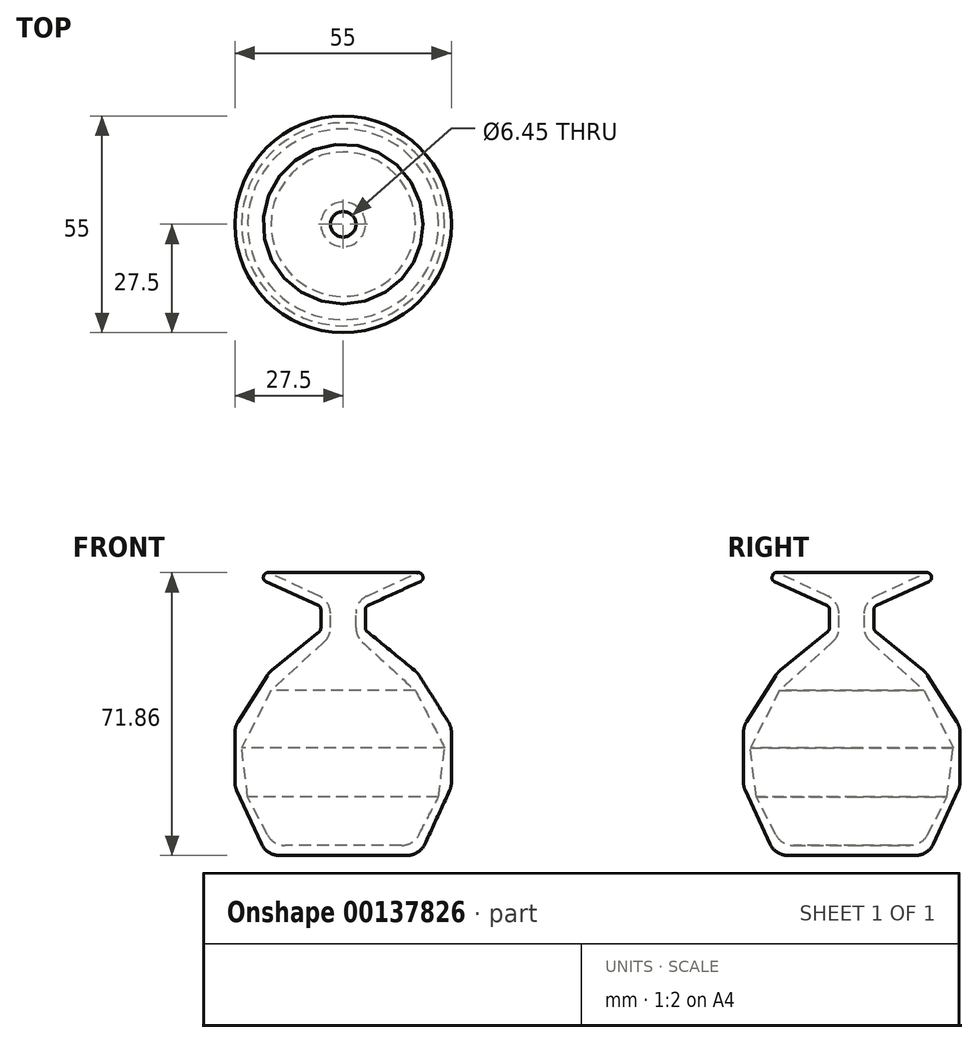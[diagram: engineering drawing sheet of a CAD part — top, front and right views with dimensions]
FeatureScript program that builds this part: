
annotation { "Feature Type Name" : "Feature", "Feature Type Description" : "" }
export const myFeature = defineFeature(function(context is Context, id is Id, definition is map)
    precondition{}
    {
        {
            var Q0;
            Q0=qCreatedBy(makeId("Front.planeOp"),FACE);
            var sketch = newSketch(context, id + "F0", { "sketchPlane" : qUnion([Q0])});
            skLineSegment(sketch, "E0", {"start": v(0, 0) * mm, "end": v(16.23, 0) * mm});
            skLineSegment(sketch, "E1", {"start": v(20.77, 2.9) * mm, "end": v(27.04, 16.49) * mm});
            skLineSegment(sketch, "E2", {"start": v(27.5, 18.58) * mm, "end": v(27.5, 31.28) * mm});
            skLineSegment(sketch, "E3", {"start": v(26.72, 33.95) * mm, "end": v(19.26, 45.78) * mm});
            skLineSegment(sketch, "E4", {"start": v(18.2, 46.99) * mm, "end": v(6.05, 56.93) * mm});
            skLineSegment(sketch, "E5", {"start": v(5.68, 57.7) * mm, "end": v(5.68, 62.57) * mm});
            skLineSegment(sketch, "E6", {"start": v(6.26, 63.48) * mm, "end": v(19.71, 69.67) * mm});
            skLineSegment(sketch, "E7", {"start": v(20.2, 71) * mm, "end": v(20.07, 71.28) * mm});
            skLineSegment(sketch, "E8", {"start": v(18.74, 71.77) * mm, "end": v(6.14, 65.97) * mm});
            skLineSegment(sketch, "E9", {"start": v(3.23, 61.43) * mm, "end": v(3.23, 57.93) * mm});
            skLineSegment(sketch, "E10", {"start": v(4.85, 54.24) * mm, "end": v(18.34, 41.87) * mm});
            skLineSegment(sketch, "E11", {"start": v(18.34, 41.87) * mm, "end": v(25.8, 27.32) * mm});
            skLineSegment(sketch, "E12", {"start": v(25.8, 27.32) * mm, "end": v(24.23, 14.85) * mm});
            skLineSegment(sketch, "E13", {"start": v(24.23, 14.85) * mm, "end": v(19.22, 5.24) * mm});
            skLineSegment(sketch, "E14", {"start": v(14.79, 2.55) * mm, "end": v(0, 2.55) * mm});
            skLineSegment(sketch, "E15", {"start": v(0, 2.55) * mm, "end": v(0, 0) * mm});
            skPoint(sketch, "E16.visualSharp", {"position": v(3.23, 64.63) * mm});
            skArc(sketch, "E16.filletArc", {"start": v(6.14, 65.97) * mm, "mid": v(4.02, 64.13) * mm, "end": v(3.23, 61.43) * mm});
            skPoint(sketch, "E17.visualSharp", {"position": v(3.23, 55.73) * mm});
            skArc(sketch, "E17.filletArc", {"start": v(3.23, 57.93) * mm, "mid": v(3.65, 55.91) * mm, "end": v(4.85, 54.24) * mm});
            skPoint(sketch, "E18.visualSharp", {"position": v(19.43, 0) * mm});
            skArc(sketch, "E18.filletArc", {"start": v(16.23, 0) * mm, "mid": v(18.92, 0.79) * mm, "end": v(20.77, 2.9) * mm});
            skPoint(sketch, "E19.visualSharp", {"position": v(27.5, 17.48) * mm});
            skArc(sketch, "E19.filletArc", {"start": v(27.04, 16.49) * mm, "mid": v(27.38, 17.5) * mm, "end": v(27.5, 18.58) * mm});
            skPoint(sketch, "E20.visualSharp", {"position": v(27.5, 32.73) * mm});
            skArc(sketch, "E20.filletArc", {"start": v(27.5, 31.28) * mm, "mid": v(27.3, 32.67) * mm, "end": v(26.72, 33.95) * mm});
            skPoint(sketch, "E21.visualSharp", {"position": v(18.83, 46.47) * mm});
            skArc(sketch, "E21.filletArc", {"start": v(19.26, 45.78) * mm, "mid": v(18.78, 46.43) * mm, "end": v(18.2, 46.99) * mm});
            skPoint(sketch, "E22.visualSharp", {"position": v(17.82, 2.55) * mm});
            skArc(sketch, "E22.filletArc", {"start": v(14.79, 2.55) * mm, "mid": v(17.38, 3.27) * mm, "end": v(19.22, 5.24) * mm});
            skPoint(sketch, "E23.visualSharp", {"position": v(5.68, 63.2) * mm});
            skArc(sketch, "E23.filletArc", {"start": v(6.26, 63.48) * mm, "mid": v(5.84, 63.1) * mm, "end": v(5.68, 62.57) * mm});
            skPoint(sketch, "E24.visualSharp", {"position": v(5.68, 57.23) * mm});
            skArc(sketch, "E24.filletArc", {"start": v(5.68, 57.7) * mm, "mid": v(5.77, 57.28) * mm, "end": v(6.05, 56.93) * mm});
            skPoint(sketch, "E25.visualSharp", {"position": v(20.62, 70.08) * mm});
            skArc(sketch, "E25.filletArc", {"start": v(19.71, 69.67) * mm, "mid": v(20.23, 70.23) * mm, "end": v(20.2, 71) * mm});
            skPoint(sketch, "E26.visualSharp", {"position": v(19.65, 72.19) * mm});
            skArc(sketch, "E26.filletArc", {"start": v(20.07, 71.28) * mm, "mid": v(19.5, 71.8) * mm, "end": v(18.74, 71.77) * mm});
            skSolve(sketch);
        }
        {
            var Q0;
            Q0=makeQuery(id+"F0.imprint","IMPRINT",FACE,{"disambiguationData":[TD([[makeQuery(id+"F0.imprint","IMPRINT",EDGE,{"derivedFrom":sQuery(id+"F0.wireOp",EDGE,"E0")}),1.0]])]});
            var Q1;
            Q1=sQuery(id+"F0.wireOp",EDGE,"E15");
            revolve(context, id + "F1", {"entities" : qUnion([Q0]), "axis" : qUnion([Q1]), "revolveType" : RevolveType.FULL});
        }
    });
